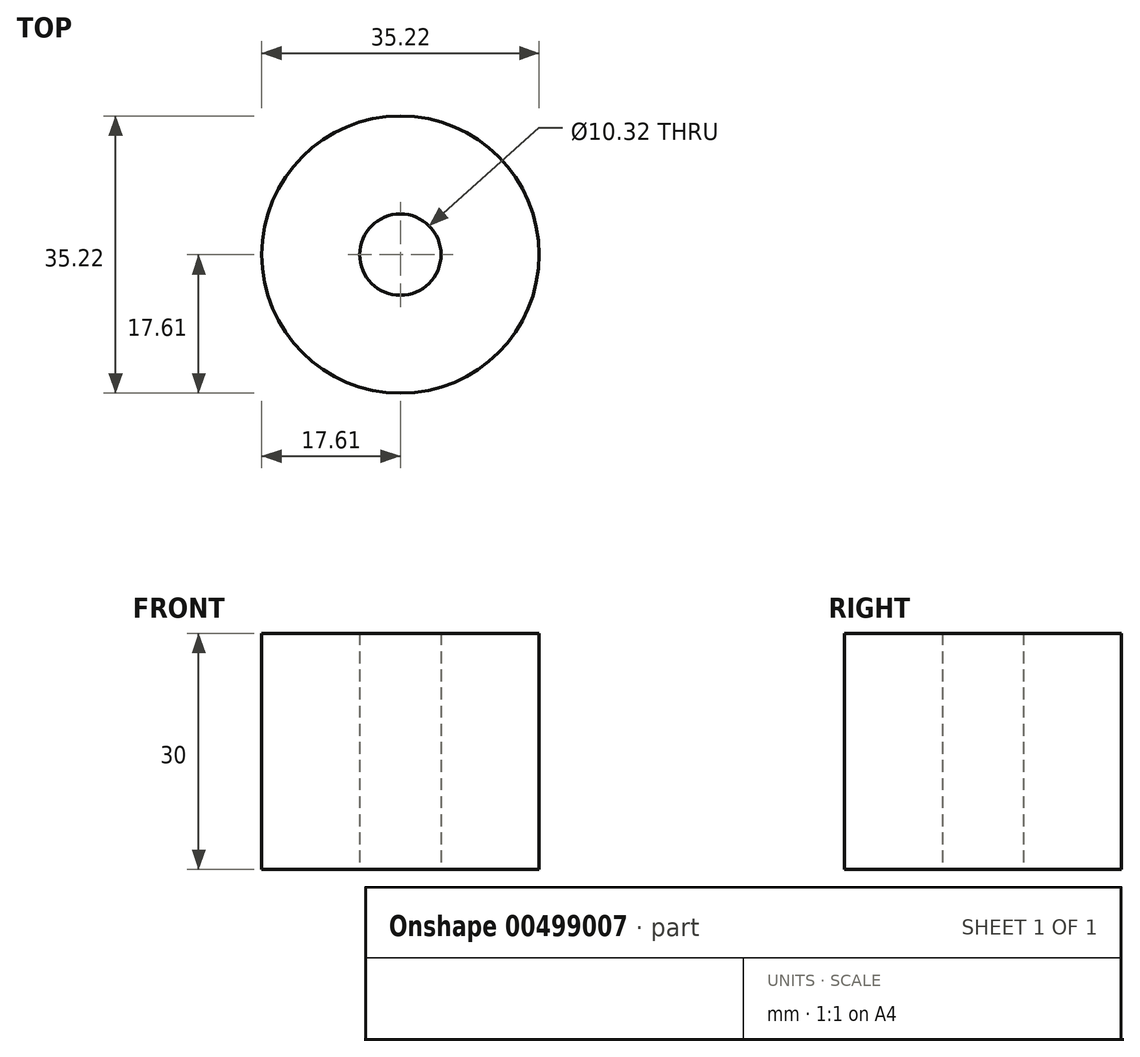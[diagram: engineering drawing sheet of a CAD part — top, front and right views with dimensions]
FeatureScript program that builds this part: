
annotation { "Feature Type Name" : "Feature", "Feature Type Description" : "" }
export const myFeature = defineFeature(function(context is Context, id is Id, definition is map)
    precondition{}
    {
        {
            var Q0;
            Q0=qCreatedBy(makeId("Top.planeOp"),FACE);
            var sketch = newSketch(context, id + "F0", { "sketchPlane" : qUnion([Q0])});
            skCircle(sketch, "E0", {"center": v(0, 0) * mm, "radius": 5.16 * mm});
            skCircle(sketch, "E1", {"center": v(0, 0) * mm, "radius": 17.6 * mm});
            skSolve(sketch);
        }
        {
            var Q0;
            Q0 = qSketchRegion(id + "F0", true);
            extrude(context, id + "F1", {"entities" : qUnion([Q0]), "depth" : 30 * mm});
        }
    });
